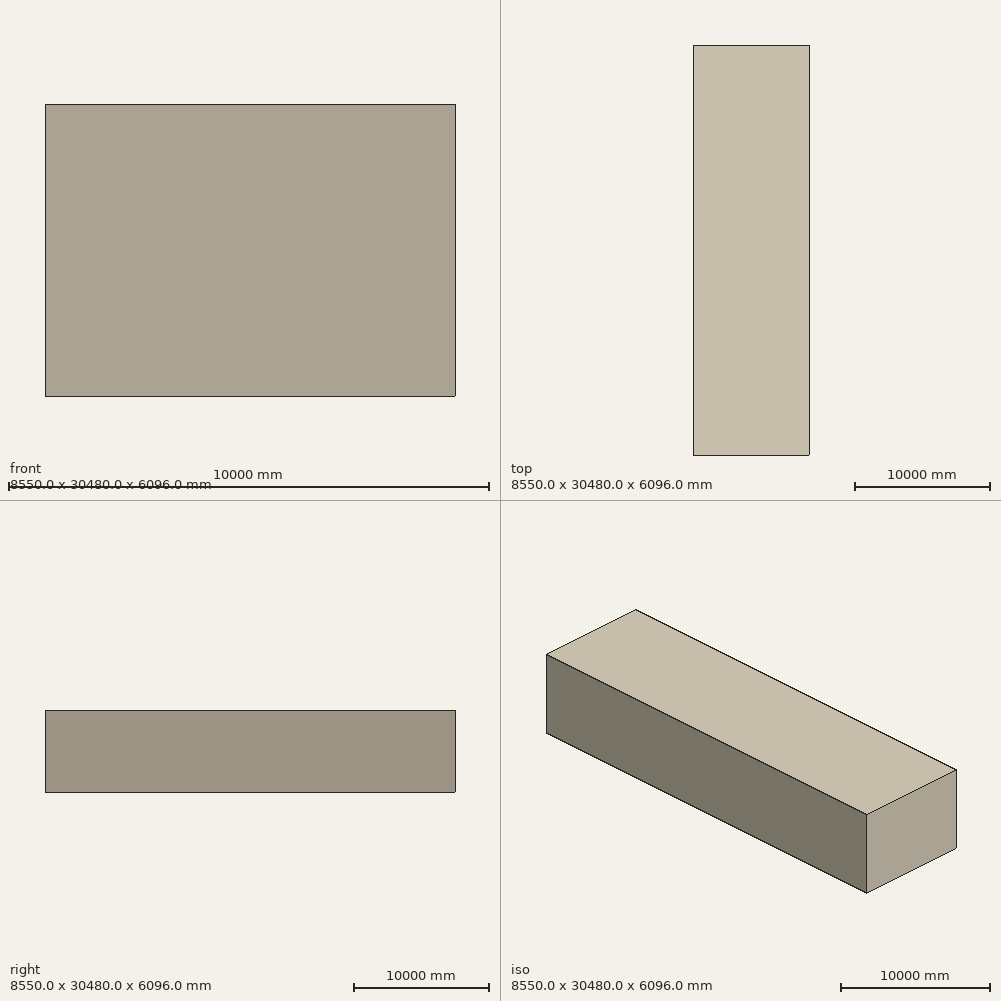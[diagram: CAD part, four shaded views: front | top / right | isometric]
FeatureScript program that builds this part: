
annotation { "Feature Type Name" : "Feature", "Feature Type Description" : "" }
export const myFeature = defineFeature(function(context is Context, id is Id, definition is map)
    precondition{}
    {
        {
            var Q0;
            Q0=qCreatedBy(makeId("Front.planeOp"),FACE);
            var sketch = newSketch(context, id + "F0", { "sketchPlane" : qUnion([Q0])});
            skLineSegment(sketch, "E0", {"start": v(-4267.07, 0) * mm, "end": v(4282.93, 0) * mm});
            skLineSegment(sketch, "E1", {"start": v(4282.93, 0) * mm, "end": v(4282.93, 6096) * mm});
            skLineSegment(sketch, "E2", {"start": v(4282.93, 6096) * mm, "end": v(-4267.07, 6096) * mm});
            skLineSegment(sketch, "E3", {"start": v(-4267.07, 6096) * mm, "end": v(-4267.07, 0) * mm});
            skSolve(sketch);
        }
        {
            var Q0;
            Q0 = qSketchRegion(id + "F0", true);
            extrude(context, id + "F1", {"entities" : qUnion([Q0]), "oppositeDirection" : true, "depth" : 30480 * mm});
        }
    });
